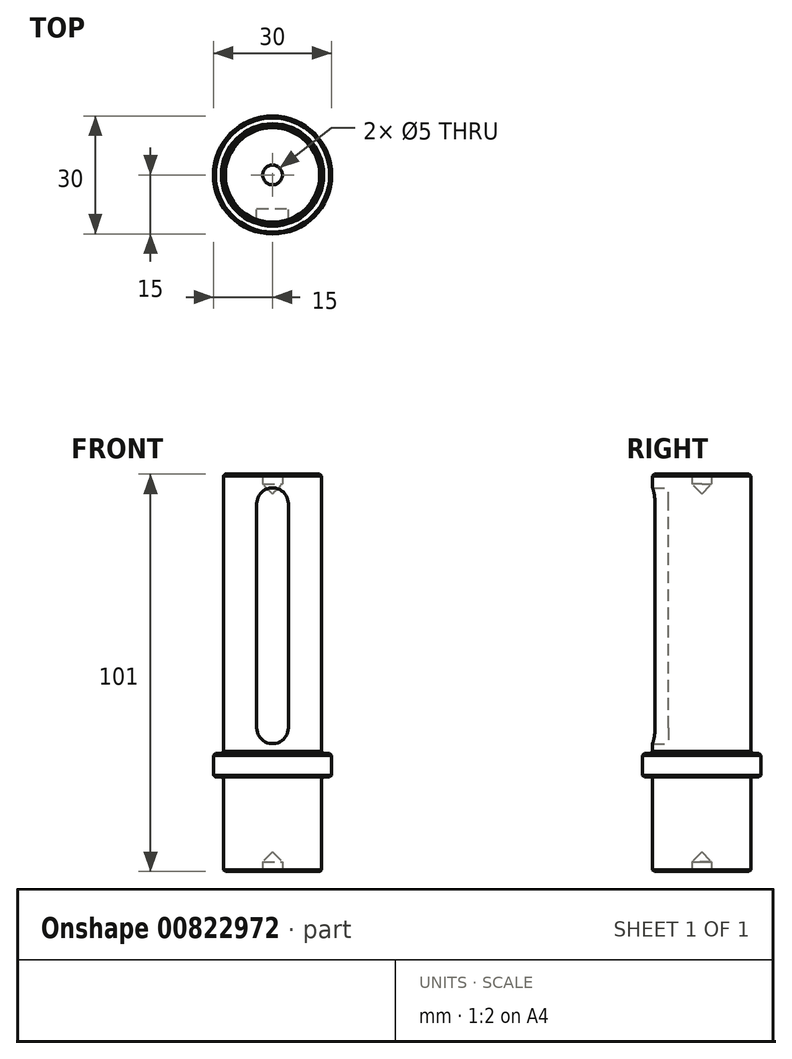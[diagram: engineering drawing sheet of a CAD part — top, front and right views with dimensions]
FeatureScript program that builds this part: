
annotation { "Feature Type Name" : "Feature", "Feature Type Description" : "" }
export const myFeature = defineFeature(function(context is Context, id is Id, definition is map)
    precondition{}
    {
        {
            var Q0;
            Q0=qCreatedBy(makeId("Front.planeOp"),FACE);
            var sketch = newSketch(context, id + "F0", { "sketchPlane" : qUnion([Q0])});
            skLineSegment(sketch, "E0", {"start": v(0, 0) * mm, "end": v(0, 15) * mm});
            skLineSegment(sketch, "E1", {"start": v(0, 15) * mm, "end": v(2.5, 17.5) * mm});
            skLineSegment(sketch, "E2", {"start": v(2.5, 17.5) * mm, "end": v(2.5, 20) * mm});
            skLineSegment(sketch, "E3", {"start": v(2.5, 20) * mm, "end": v(12.5, 20) * mm});
            skLineSegment(sketch, "E4", {"start": v(12.5, 20) * mm, "end": v(12.5, 17.1) * mm});
            skLineSegment(sketch, "E5", {"start": v(12.5, 17.1) * mm, "end": v(12.5, 17.1) * mm});
            skLineSegment(sketch, "E6", {"start": v(12.5, 17.1) * mm, "end": v(12.5, 16) * mm});
            skLineSegment(sketch, "E7", {"start": v(12.5, 16) * mm, "end": v(12.5, 16) * mm});
            skLineSegment(sketch, "E8", {"start": v(12.5, 16) * mm, "end": v(12.5, -51) * mm});
            skLineSegment(sketch, "E9", {"start": v(12.5, -51) * mm, "end": v(15, -51) * mm});
            skLineSegment(sketch, "E10", {"start": v(15, -51) * mm, "end": v(15, -55.7) * mm});
            skLineSegment(sketch, "E11", {"start": v(15, -55.7) * mm, "end": v(15, -55.7) * mm});
            skLineSegment(sketch, "E12", {"start": v(15, -55.7) * mm, "end": v(15, -57) * mm});
            skLineSegment(sketch, "E13", {"start": v(12.5, -57) * mm, "end": v(15, -57) * mm});
            skLineSegment(sketch, "E14", {"start": v(12.5, -57) * mm, "end": v(12.5, -77) * mm});
            skLineSegment(sketch, "E15", {"start": v(12.5, -77) * mm, "end": v(12.5, -77) * mm});
            skLineSegment(sketch, "E16", {"start": v(12.5, -77) * mm, "end": v(12.5, -78.3) * mm});
            skLineSegment(sketch, "E17", {"start": v(12.5, -78.3) * mm, "end": v(12.5, -78.3) * mm});
            skLineSegment(sketch, "E18", {"start": v(12.5, -78.3) * mm, "end": v(12.5, -81) * mm});
            skLineSegment(sketch, "E19", {"start": v(2.5, -81) * mm, "end": v(2.5, -78.5) * mm});
            skLineSegment(sketch, "E20", {"start": v(2.5, -78.5) * mm, "end": v(0, -76) * mm});
            skLineSegment(sketch, "E21", {"start": v(0, -76) * mm, "end": v(0, 0) * mm});
            skLineSegment(sketch, "E22", {"start": v(12.5, -81) * mm, "end": v(2.5, -81) * mm});
            skLineSegment(sketch, "E23", {"start": v(0, 15) * mm, "end": v(0, 95.93) * mm, "construction": true});
            skLineSegment(sketch, "E24", {"start": v(0, -76) * mm, "end": v(0, -104.42) * mm, "construction": true});
            skSolve(sketch);
        }
        {
            var Q0;
            Q0=qSketchRegion(id+"F0",true);
            var Q1;
            Q1=sQuery(id+"F0.wireOp",EDGE,"E23");
            revolve(context, id + "F1", {"surfaceOperationType" : NewSurfaceOperationType.NEW, "entities" : qUnion([Q0]), "axis" : qUnion([Q1]), "revolveType" : RevolveType.FULL});
        }
        {
            var Q0;
            Q0=makeQuery(id+"F1.opRevolve","SWEPT_EDGE",EDGE,{"disambiguationData":[OSD([sQuery(id+"F0.wireOp",EDGE,"E3"),sQuery(id+"F0.wireOp",EDGE,"E4")])]});
            var Q1;
            Q1=makeQuery(id+"F1.opRevolve","SWEPT_FACE",FACE,{"disambiguationData":[OSD([sQuery(id+"F0.wireOp",EDGE,"E9")])]});
            var Q2;
            Q2=makeQuery(id+"F1.opRevolve","SWEPT_EDGE",EDGE,{"disambiguationData":[OSD([sQuery(id+"F0.wireOp",EDGE,"E18"),sQuery(id+"F0.wireOp",EDGE,"E22")])]});
            var Q3;
            Q3=makeQuery(id+"F1.opRevolve","SWEPT_EDGE",EDGE,{"disambiguationData":[OSD([sQuery(id+"F0.wireOp",EDGE,"E12"),sQuery(id+"F0.wireOp",EDGE,"E13")])]});
            chamfer(context, id + "F2", {"entities" : qUnion([Q0, Q1, Q2, Q3]), "width" : 0.5 * mm, "tangentPropagation" : true});
        }
        {
            var Q0;
            Q0=makeQuery(id+"F1.opRevolve","SWEPT_EDGE",EDGE,{"disambiguationData":[OSD([sQuery(id+"F0.wireOp",EDGE,"E13"),sQuery(id+"F0.wireOp",EDGE,"E14")])]});
            fillet(context, id + "F3", {"entities" : qUnion([Q0]), "radius" : 0.5 * mm, "tangentPropagation" : true, "allowEdgeOverflow" : false});
        }
        {
            var Q0;
            Q0=qCreatedBy(makeId("Front.planeOp"),FACE);
            cPlane(context, id + "F4", {"entities" : qUnion([Q0]), "cplaneType" : CPlaneType.OFFSET, "offset" : 8.5 * mm, "width" : 150 * mm, "height" : 150 * mm});
        }
        {
            var Q0;
            Q0=qCreatedBy(id+"F4.planeOp",FACE);
            var sketch = newSketch(context, id + "F5", { "sketchPlane" : qUnion([Q0])});
            skLineSegment(sketch, "E25", {"start": v(0, 0) * mm, "end": v(0, 12.5) * mm, "construction": true});
            skLineSegment(sketch, "E26", {"start": v(0, -44.5) * mm, "end": v(0, 0) * mm, "construction": true});
            skArc(sketch, "E27", {"start": v(4, 12.5) * mm, "mid": v(0, 16.5) * mm, "end": v(-4, 12.5) * mm});
            skArc(sketch, "E28", {"start": v(-4, -44.5) * mm, "mid": v(0, -48.5) * mm, "end": v(4, -44.5) * mm});
            skLineSegment(sketch, "E29.1", {"start": v(-14.5, -51) * mm, "end": v(14.5, -51) * mm, "construction": true});
            skLineSegment(sketch, "E30", {"start": v(4, -44.5) * mm, "end": v(4, 12.5) * mm});
            skLineSegment(sketch, "E31", {"start": v(-4, 12.5) * mm, "end": v(-4, -44.5) * mm});
            skLineSegment(sketch, "E32.0", {"start": v(-12, 20) * mm, "end": v(12, 20) * mm, "construction": true});
            skSolve(sketch);
        }
        {
            var Q0;
            Q0=qSketchRegion(id+"F5",true);
            extrude(context, id + "F6", {"entities" : qUnion([Q0]), "operationType" : NewBodyOperationType.REMOVE, "depth" : 4 * mm, "offsetDistance" : 25 * mm});
        }
    });
